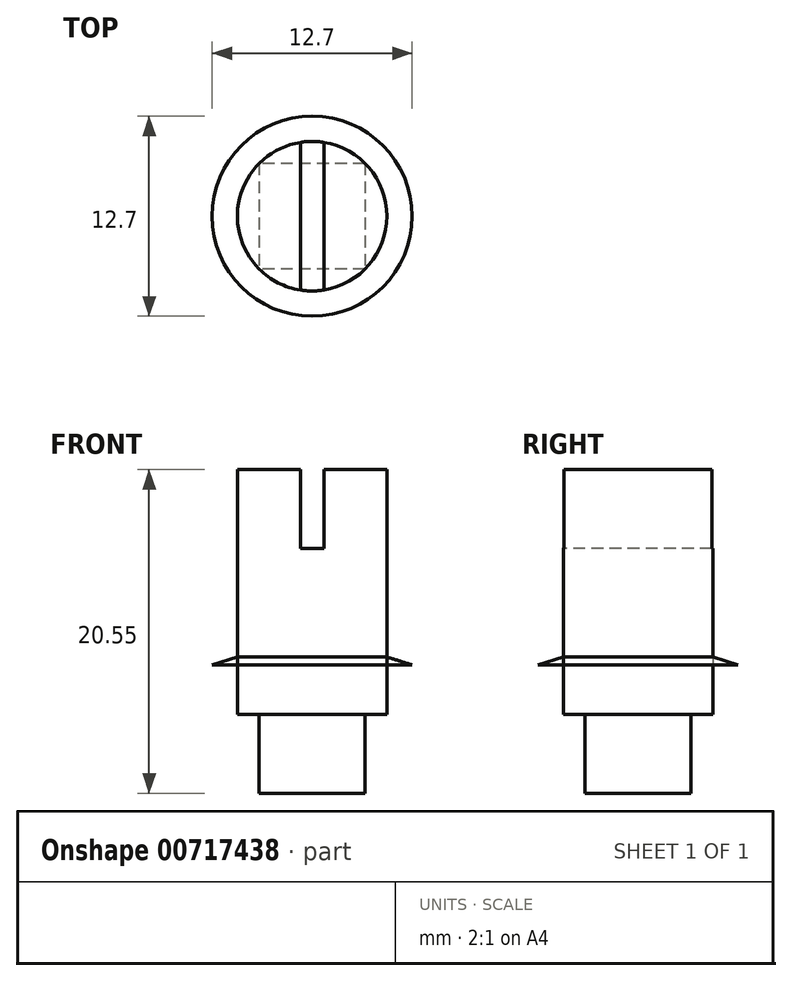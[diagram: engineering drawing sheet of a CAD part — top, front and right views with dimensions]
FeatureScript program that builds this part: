
annotation { "Feature Type Name" : "Feature", "Feature Type Description" : "" }
export const myFeature = defineFeature(function(context is Context, id is Id, definition is map)
    precondition{}
    {
        {
            var Q0;
            Q0=qCreatedBy(makeId("Top.planeOp"),FACE);
            var sketch = newSketch(context, id + "F0", { "sketchPlane" : qUnion([Q0])});
            skCircle(sketch, "E0", {"center": v(0, 0) * mm, "radius": 4.75 * mm});
            skSolve(sketch);
        }
        {
            var Q0;
            Q0 = qSketchRegion(id + "F0", true);
            extrude(context, id + "F1", {"entities" : qUnion([Q0]), "depth" : 20.55 * mm, "offsetDistance" : 25.4 * mm});
        }
        {
            var Q0;
            Q0=qCreatedBy(makeId("Top.planeOp"),FACE);
            cPlane(context, id + "F2", {"entities" : qUnion([Q0]), "cplaneType" : CPlaneType.OFFSET, "offset" : 20.55 * mm, "width" : 152.4 * mm, "height" : 152.4 * mm});
        }
        {
            var Q0;
            Q0=qCreatedBy(id+"F2.planeOp",FACE);
            var sketch = newSketch(context, id + "F3", { "sketchPlane" : qUnion([Q0])});
            skLineSegment(sketch, "E1.bottom", {"start": v(0.75, 5.36) * mm, "end": v(-0.75, 5.36) * mm});
            skLineSegment(sketch, "E1.top", {"start": v(0.75, -5.36) * mm, "end": v(-0.75, -5.36) * mm});
            skLineSegment(sketch, "E1.left", {"start": v(0.75, 5.36) * mm, "end": v(0.75, -5.36) * mm});
            skLineSegment(sketch, "E1.right", {"start": v(-0.75, 5.36) * mm, "end": v(-0.75, -5.36) * mm});
            skPoint(sketch, "E1.middle", {"position": v(0, 0) * mm});
            skSolve(sketch);
        }
        {
            var Q0;
            Q0=qCreatedBy(makeId("Top.planeOp"),FACE);
            var sketch = newSketch(context, id + "F4", { "sketchPlane" : qUnion([Q0])});
            skLineSegment(sketch, "E2.bottom", {"start": v(4.8, 4.8) * mm, "end": v(-4.8, 4.8) * mm});
            skLineSegment(sketch, "E2.top", {"start": v(4.8, -4.8) * mm, "end": v(-4.8, -4.8) * mm});
            skLineSegment(sketch, "E2.left", {"start": v(4.8, 4.8) * mm, "end": v(4.8, -4.8) * mm});
            skLineSegment(sketch, "E2.right", {"start": v(-4.8, 4.8) * mm, "end": v(-4.8, -4.8) * mm});
            skPoint(sketch, "E2.middle", {"position": v(0, 0) * mm});
            skSolve(sketch);
        }
        {
            var Q0;
            Q0 = qSketchRegion(id + "F4", true);
            extrude(context, id + "F5", {"entities" : qUnion([Q0]), "operationType" : NewBodyOperationType.REMOVE, "depth" : 5 * mm, "offsetDistance" : 25.4 * mm});
        }
        {
            var Q0;
            Q0 = qSketchRegion(id + "F3", true);
            extrude(context, id + "F6", {"entities" : qUnion([Q0]), "operationType" : NewBodyOperationType.REMOVE, "oppositeDirection" : true, "depth" : 5 * mm, "offsetDistance" : 25.4 * mm});
        }
        {
            var Q0;
            Q0=qCreatedBy(makeId("Top.planeOp"),FACE);
            var sketch = newSketch(context, id + "F7", { "sketchPlane" : qUnion([Q0])});
            skLineSegment(sketch, "E3.bottom", {"start": v(3.36, 3.36) * mm, "end": v(-3.36, 3.36) * mm});
            skLineSegment(sketch, "E3.top", {"start": v(3.36, -3.36) * mm, "end": v(-3.36, -3.36) * mm});
            skLineSegment(sketch, "E3.left", {"start": v(3.36, 3.36) * mm, "end": v(3.36, -3.36) * mm});
            skLineSegment(sketch, "E3.right", {"start": v(-3.36, 3.36) * mm, "end": v(-3.36, -3.36) * mm});
            skPoint(sketch, "E3.middle", {"position": v(0, 0) * mm});
            skSolve(sketch);
        }
        {
            var Q0;
            Q0 = qSketchRegion(id + "F7", true);
            extrude(context, id + "F8", {"entities" : qUnion([Q0]), "operationType" : NewBodyOperationType.ADD, "depth" : 5 * mm, "offsetDistance" : 25.4 * mm});
        }
        {
            var Q0;
            Q0=qCreatedBy(makeId("Top.planeOp"),FACE);
            cPlane(context, id + "F9", {"entities" : qUnion([Q0]), "cplaneType" : CPlaneType.OFFSET, "offset" : 8.15 * mm, "width" : 152.4 * mm, "height" : 152.4 * mm});
        }
        {
            var Q0;
            Q0=qCreatedBy(id+"F9.planeOp",FACE);
            var sketch = newSketch(context, id + "F10", { "sketchPlane" : qUnion([Q0])});
            skCircle(sketch, "E4", {"center": v(0, 0) * mm, "radius": 6.35 * mm});
            skSolve(sketch);
        }
        {
            var Q0;
            Q0=qCreatedBy(makeId("Top.planeOp"),FACE);
            cPlane(context, id + "F11", {"entities" : qUnion([Q0]), "cplaneType" : CPlaneType.OFFSET, "offset" : 8.65 * mm, "width" : 152.4 * mm, "height" : 152.4 * mm});
        }
        {
            var Q0;
            Q0=qCreatedBy(id+"F11.planeOp",FACE);
            var sketch = newSketch(context, id + "F12", { "sketchPlane" : qUnion([Q0])});
            skCircle(sketch, "E5", {"center": v(0, 0) * mm, "radius": 4.75 * mm});
            skSolve(sketch);
        }
        {
            var Q0;
            Q0=makeQuery(id+"F10.imprint","IMPRINT",FACE,{"disambiguationData":[TD([[makeQuery(id+"F10.imprint","IMPRINT",EDGE,{"derivedFrom":sQuery(id+"F10.wireOp",EDGE,"E4")}),1.0]])]});
            var Q1;
            Q1=makeQuery(id+"F12.imprint","IMPRINT",FACE,{"disambiguationData":[TD([[makeQuery(id+"F12.imprint","IMPRINT",EDGE,{"derivedFrom":sQuery(id+"F12.wireOp",EDGE,"E5")}),1.0]])]});
            loft(context, id + "F13", {"sheetProfilesArray" : [{ "sheetProfileEntities" : qUnion([Q0]) }, { "sheetProfileEntities" : qUnion([Q1]) }]});
        }
    });
